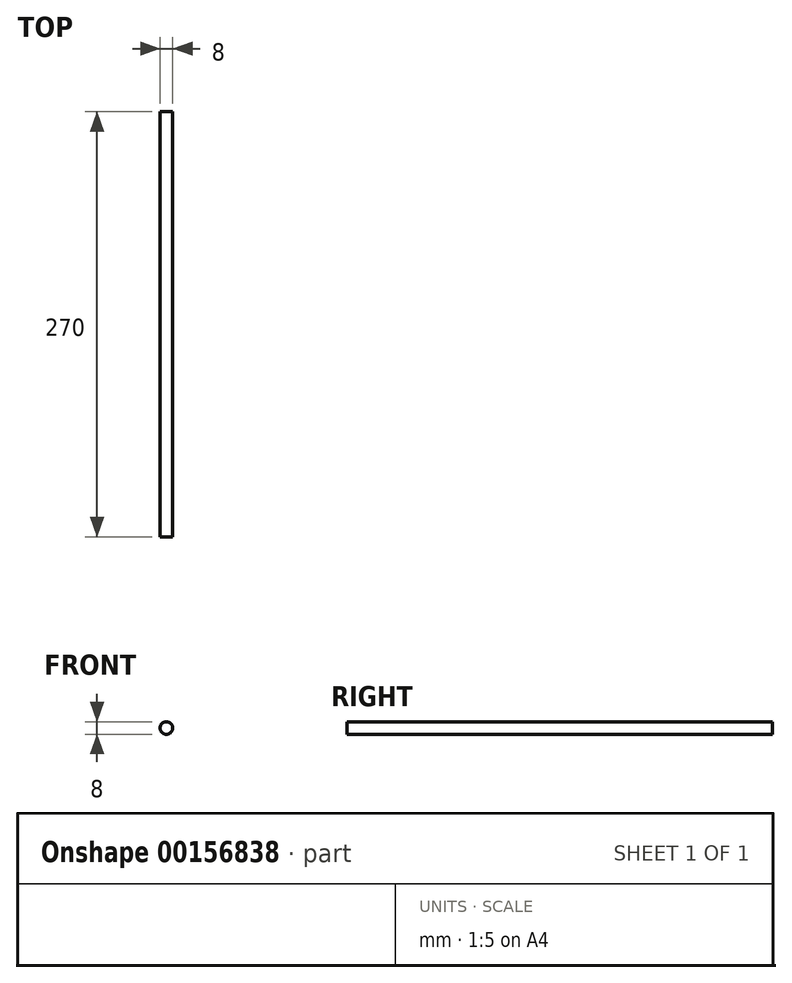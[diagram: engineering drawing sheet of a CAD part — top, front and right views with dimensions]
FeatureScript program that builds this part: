
annotation { "Feature Type Name" : "Feature", "Feature Type Description" : "" }
export const myFeature = defineFeature(function(context is Context, id is Id, definition is map)
    precondition{}
    {
        {
            var Q0;
            Q0=qCreatedBy(makeId("Front.planeOp"),FACE);
            var sketch = newSketch(context, id + "F0", { "sketchPlane" : qUnion([Q0])});
            skCircle(sketch, "E0", {"center": v(0, 0) * mm, "radius": 4 * mm});
            skSolve(sketch);
        }
        {
            var Q0;
            Q0=qSketchRegion(id+"F0",true);
            extrude(context, id + "F1", {"entities" : qUnion([Q0]), "endBound" : BoundingType.SYMMETRIC, "depth" : 270 * mm});
        }
    });
